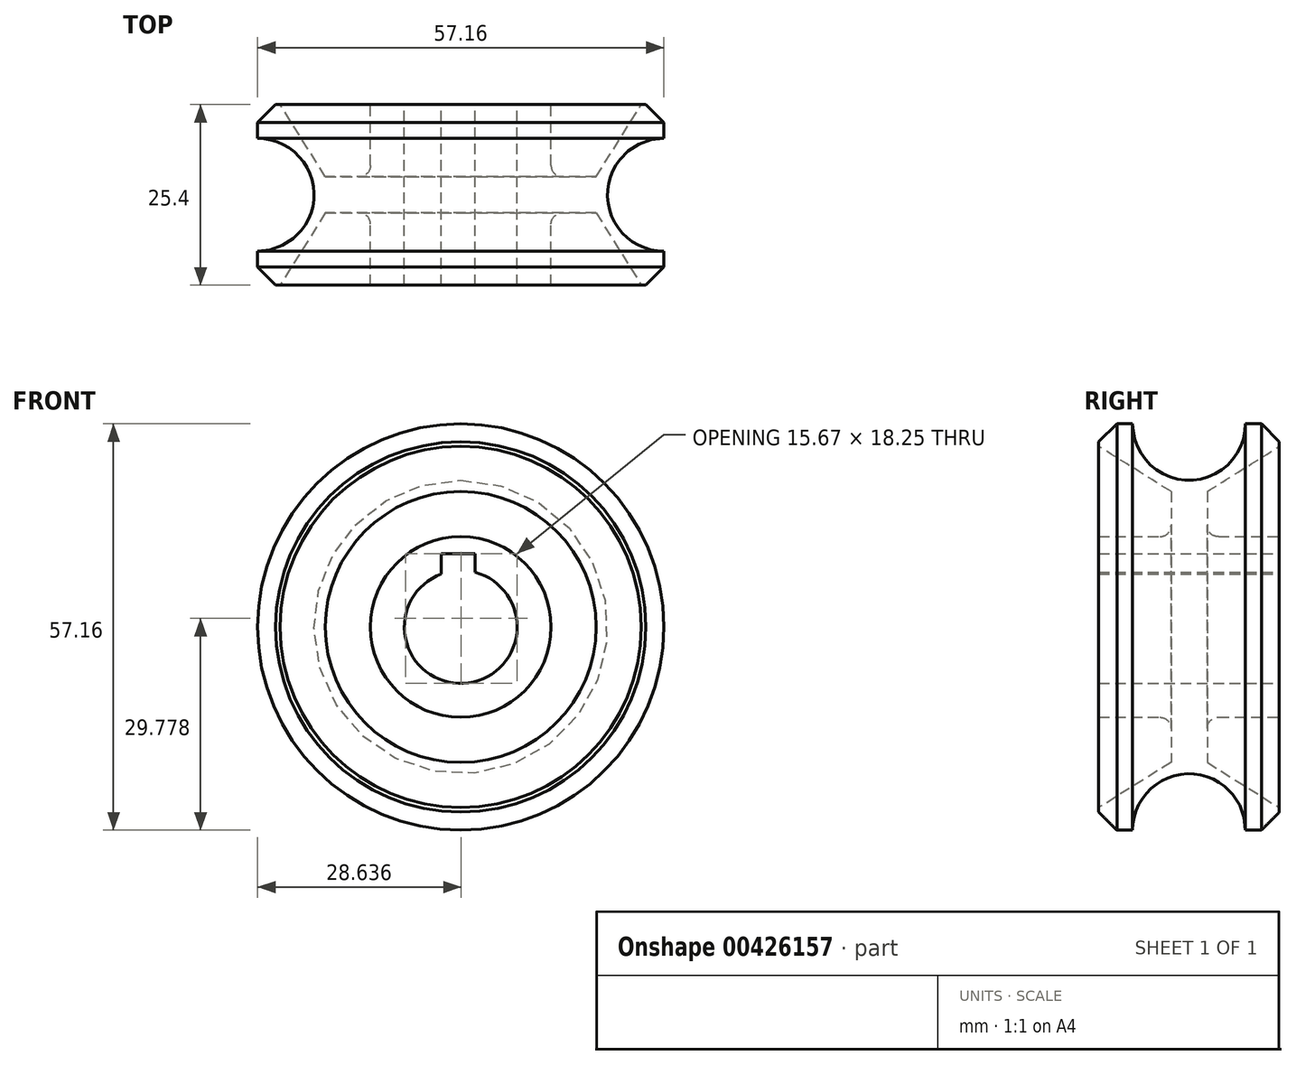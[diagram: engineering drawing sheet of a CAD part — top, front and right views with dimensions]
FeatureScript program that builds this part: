
annotation { "Feature Type Name" : "Feature", "Feature Type Description" : "" }
export const myFeature = defineFeature(function(context is Context, id is Id, definition is map)
    precondition{}
    {
        {
            var Q0;
            Q0=qCreatedBy(makeId("Front.planeOp"),FACE);
            var sketch = newSketch(context, id + "F0", { "sketchPlane" : qUnion([Q0])});
            skCircle(sketch, "E0", {"center": v(0, 0) * mm, "radius": 7.94 * mm});
            skCircle(sketch, "E1", {"center": v(0, 0) * mm, "radius": 28.58 * mm});
            skSolve(sketch);
        }
        {
            var Q0;
            Q0 = qSketchRegion(id + "F0", true);
            var Q1;
            Q1=makeQuery(id+"F0.imprint","IMPRINT",FACE,{"disambiguationData":[TD([[makeQuery(id+"F0.imprint","IMPRINT",EDGE,{"derivedFrom":sQuery(id+"F0.wireOp",EDGE,"E0")}),-1.0]])]});
            extrude(context, id + "F1", {"entities" : qUnion([Q0, Q1]), "depth" : 12.7 * mm, "hasSecondDirection" : true, "secondDirectionOppositeDirection" : true, "secondDirectionDepth" : 12.7 * mm});
        }
        {
            var Q0;
            Q0=qCreatedBy(makeId("Right.planeOp"),FACE);
            var sketch = newSketch(context, id + "F2", { "sketchPlane" : qUnion([Q0])});
            skLineSegment(sketch, "E2", {"start": v(0, 0) * mm, "end": v(133.27, 0) * mm, "construction": true});
            skCircle(sketch, "E3", {"center": v(0, 28.58) * mm, "radius": 7.94 * mm});
            skSolve(sketch);
        }
        {
            var Q0;
            Q0 = qSketchRegion(id + "F2", true);
            var Q1;
            Q1=sQuery(id+"F2.wireOp",EDGE,"E2");
            revolve(context, id + "F3", {"operationType" : NewBodyOperationType.REMOVE, "entities" : qUnion([Q0]), "axis" : qUnion([Q1]), "revolveType" : RevolveType.FULL, "oppositeDirection" : true});
        }
        {
            var Q0;
            Q0=qCreatedBy(makeId("Right.planeOp"),FACE);
            var sketch = newSketch(context, id + "F4", { "sketchPlane" : qUnion([Q0])});
            skLineSegment(sketch, "E4", {"start": v(0, 0) * mm, "end": v(48.2, 0) * mm, "construction": true});
            skLineSegment(sketch, "E5", {"start": v(2.54, 12.7) * mm, "end": v(12.7, 12.7) * mm});
            skLineSegment(sketch, "E6", {"start": v(12.7, 12.7) * mm, "end": v(12.7, 25.4) * mm});
            skLineSegment(sketch, "E7", {"start": v(12.7, 25.4) * mm, "end": v(2.54, 19.05) * mm});
            skLineSegment(sketch, "E8", {"start": v(2.54, 19.05) * mm, "end": v(2.54, 12.7) * mm});
            skLineSegment(sketch, "E9", {"start": v(0, 0) * mm, "end": v(0, 27.61) * mm, "construction": true});
            skLineSegment(sketch, "E10.MirrorCS", {"start": v(-2.54, 12.7) * mm, "end": v(-12.7, 12.7) * mm});
            skLineSegment(sketch, "E11.MirrorCS", {"start": v(-2.54, 19.05) * mm, "end": v(-2.54, 12.7) * mm});
            skLineSegment(sketch, "E12.MirrorCS", {"start": v(-12.7, 25.4) * mm, "end": v(-2.54, 19.05) * mm});
            skLineSegment(sketch, "E13.MirrorCS", {"start": v(-12.7, 12.7) * mm, "end": v(-12.7, 25.4) * mm});
            skSolve(sketch);
        }
        {
            var Q0;
            Q0 = qSketchRegion(id + "F4", true);
            var Q1;
            Q1=sQuery(id+"F4.wireOp",EDGE,"E4");
            revolve(context, id + "F5", {"operationType" : NewBodyOperationType.REMOVE, "entities" : qUnion([Q0]), "axis" : qUnion([Q1]), "revolveType" : RevolveType.FULL, "oppositeDirection" : true});
        }
        {
            var Q0;
            Q0=makeQuery(id+"F1.opExtrude","CAP_EDGE",EDGE,{"disambiguationData":[OSD([sQuery(id+"F0.wireOp",EDGE,"E1")])],"isStart":true});
            var Q1;
            Q1=makeQuery(id+"F1.opExtrude","CAP_EDGE",EDGE,{"disambiguationData":[OSD([sQuery(id+"F0.wireOp",EDGE,"E1")])],"isStart":false});
            chamfer(context, id + "F6", {"entities" : qUnion([Q0, Q1]), "chamferType" : ChamferType.OFFSET_ANGLE, "width" : 2.54 * mm, "oppositeDirection" : false, "angle" : 45 * degree, "tangentPropagation" : true});
        }
        {
            var Q0;
            Q0=makeQuery(id+"F5.boolean.opBoolean","COPY",EDGE,{"derivedFrom":makeQuery(id+"F5.opRevolve","SWEPT_EDGE",EDGE,{"disambiguationData":[OSD([sQuery(id+"F4.wireOp",EDGE,"E5"),sQuery(id+"F4.wireOp",EDGE,"E8")])]})});
            var Q1;
            Q1=makeQuery(id+"F5.boolean.opBoolean","COPY",EDGE,{"derivedFrom":makeQuery(id+"F5.opRevolve","SWEPT_EDGE",EDGE,{"disambiguationData":[OSD([sQuery(id+"F4.wireOp",EDGE,"E10.MirrorCS"),sQuery(id+"F4.wireOp",EDGE,"E11.MirrorCS")])]})});
            fillet(context, id + "F7", {"entities" : qUnion([Q0, Q1]), "radius" : 1.59 * mm, "tangentPropagation" : true, "allowEdgeOverflow" : false});
        }
        {
            var Q0;
            Q0=qCreatedBy(makeId("Front.planeOp"),FACE);
            var sketch = newSketch(context, id + "F8", { "sketchPlane" : qUnion([Q0])});
            skLineSegment(sketch, "E14.bottom", {"start": v(2.04, 10.33) * mm, "end": v(-2.74, 10.33) * mm});
            skLineSegment(sketch, "E14.top", {"start": v(2.04, 0) * mm, "end": v(-2.74, 0) * mm});
            skLineSegment(sketch, "E14.left", {"start": v(2.04, 10.33) * mm, "end": v(2.04, 0) * mm});
            skLineSegment(sketch, "E14.right", {"start": v(-2.74, 10.33) * mm, "end": v(-2.74, 0) * mm});
            skSolve(sketch);
        }
        {
            var Q0;
            Q0 = qSketchRegion(id + "F8", true);
            extrude(context, id + "F9", {"entities" : qUnion([Q0]), "operationType" : NewBodyOperationType.REMOVE, "depth" : 15.42 * mm, "hasSecondDirection" : true, "secondDirectionOppositeDirection" : true, "secondDirectionDepth" : 13.72 * mm});
        }
    });
